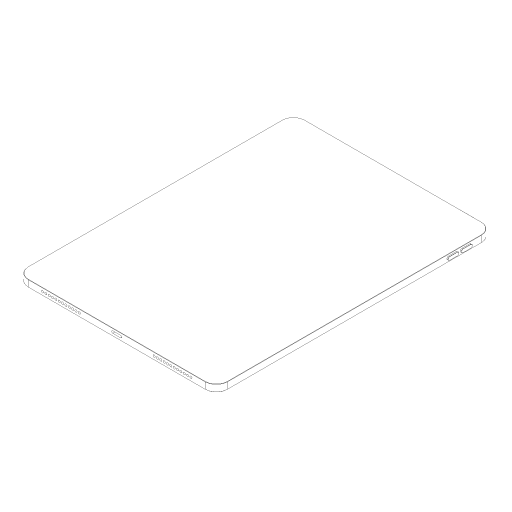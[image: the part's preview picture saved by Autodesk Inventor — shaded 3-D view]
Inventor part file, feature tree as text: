
AUTODESK INVENTOR PART (.ipt)
format: ipt  version: 2024 (Build 280153000, 153)  size: 295,424 bytes
history: native  units: mm
features: extrude x8, sketch x6, fillet x5
ambient origin geometry x8: Origin, YZ Plane, XZ Plane, XY Plane, X Axis, Y Axis, Z Axis, Center Point
bodies: Solid1 (feature_tree)
feature tree (19):
  extrude  "Extrusion1"  Depth=247.6mm
  fillet  "Fillet1"  Radius=6.1mm
  extrude  "Extrusion2"  Depth=7.0mm
  sketch  "Sketch3"  dims[d6=3.0mm d8=7.0mm d9=3.0mm]
  extrude  "Extrusion3"  Depth=7.0mm
  extrude  "Extrusion4"  Depth=2.0mm
  sketch  "Sketch4"  dims[d10=2.0mm d11=9.0mm]
  extrude  "Extrusion5"  Depth=1.0mm
  extrude  "Extrusion6"  Depth=0.1mm
  extrude  "Extrusion7"  Depth=1.0mm TaperAngle=0.0deg
  fillet  "Fillet2"  Radius=2.0mm
  extrude  "Extrusion8"  Depth=3.0mm
  fillet  "Fillet3"  Radius=6.0mm
  fillet  "Fillet4"  Radius=2.0mm
  fillet  "Fillet5"  Radius=3.0mm
  sketch  "Sketch1"  dims[d0=178.5mm d1=247.6mm d2=6.1mm d3=0.0mm]
  sketch  "Sketch2"  dims[d4=10.0mm d5=7.0mm]
  sketch  "Sketch5"  dims[d12=1.0mm d13=0.0mm d14=13.0mm]
  sketch  "Sketch6"  dims[d15=4.0mm d16=5.0mm d17=1.0mm d18=0.0mm d19=2.0mm d20=90.0mm d22=3.0mm d23=10.0mm d25=10.0mm d27=6.0mm d28=2.0mm d29=90.0mm d31=3.0mm d32=10.0mm d34=10.0mm d37=26.0mm d38=40.0mm d40=3.0mm d41=10.0mm d43=10.0mm d45=2.0mm d46=0.0mm d47=7.0mm d48=2.0mm d49=2.0mm d50=29.0mm d51=120.0mm d53=3.0mm d54=10.0mm d56=10.0mm d58=2.0mm d59=29.0mm d60=120.0mm d62=3.0mm d63=10.0mm d65=10.0mm d67=2.0mm d68=0.0mm d69=6.0mm d70=0.0mm d71=1.0mm d72=4.0mm d73=0.0mm d74=0.2mm d75=10.0mm d76=12.0mm d77=13.0mm d78=13.0mm d79=2.0mm d80=0.0mm d81=1.0mm d82=0.2mm d83=0.1mm]
